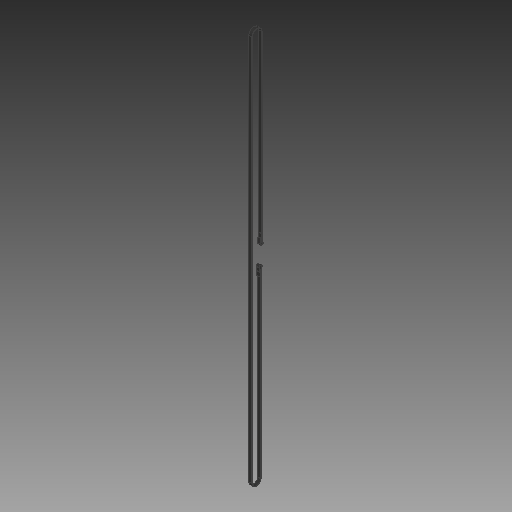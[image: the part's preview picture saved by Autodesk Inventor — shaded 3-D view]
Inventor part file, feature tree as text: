
AUTODESK INVENTOR PART (.ipt)
format: ipt  version: 2017 SP1 (Build 210196100, 196)  size: 157,184 bytes
history: native  units: in
note: dims shown in document units (in); Inventor stores cm internally (conversion verified against a paired STEP export)
features: extrude x1, sketch x1
ambient origin geometry x8: Origin, YZ Plane, XZ Plane, XY Plane, X Axis, Y Axis, Z Axis, Center Point
bodies: Solid1 (feature_tree)
feature tree (2):
  extrude  "Extrusion1"  Depth=0.5in
  sketch  "Sketch1"  dims[d1=0.5625in d2=0.5in d4=0.25in d5=0.0625in d6=2.375in d7=0.25in d8=0.5in d9=0.5in d10=0.005in d11=0.25in d12=0.5in d13=0.005in d14=0.5in d15=47.0in d16=0.375in d17=0.0in]
